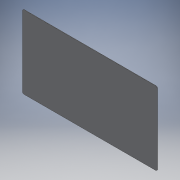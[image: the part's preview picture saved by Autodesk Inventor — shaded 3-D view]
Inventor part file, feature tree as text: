
AUTODESK INVENTOR PART (.ipt)
format: ipt  version: 2019 (Build 230136000, 136)  size: 96,768 bytes
history: native  units: mm
features: other x5, reference x4, extrude x1, sketch x1, helix x1
ambient origin geometry x8: Origin, YZ Plane, XZ Plane, XY Plane, X Axis, Y Axis, Z Axis, Center Point
bodies: Solid1 (feature_tree)
feature tree (12):
  extrude  "Extrusion1"  Depth=3.0mm TaperAngle=0.0deg
  sketch  "Sketch1"  dims[d0=10.0mm d1=3.0mm d2=0.0mm]
  reference  "Reference1"
  reference  "Reference2"
  reference  "Reference3"
  reference  "Reference4"
  other  "<userpath>\Documents\CAD Files\Helix DLP\Helix DLP.iam"
  helix  "Helix DLP.iam"  [1 undecoded]
  other  "30X30 - T-slot - Aluminium Profile_CPY_CPY:1"
  other  "30X30 - T-slot - Aluminium Profile:6"
  other  "30X30 - T-slot - Aluminium Profile:3"
  other  "30X30 - T-slot - Aluminium Profile_CPY_CPY:3"
note: 1 required parameter value undecoded (feature->parameter linkage not recoverable at this tier; creation-order binding heuristic only, values carry confidence <= 0.55)
